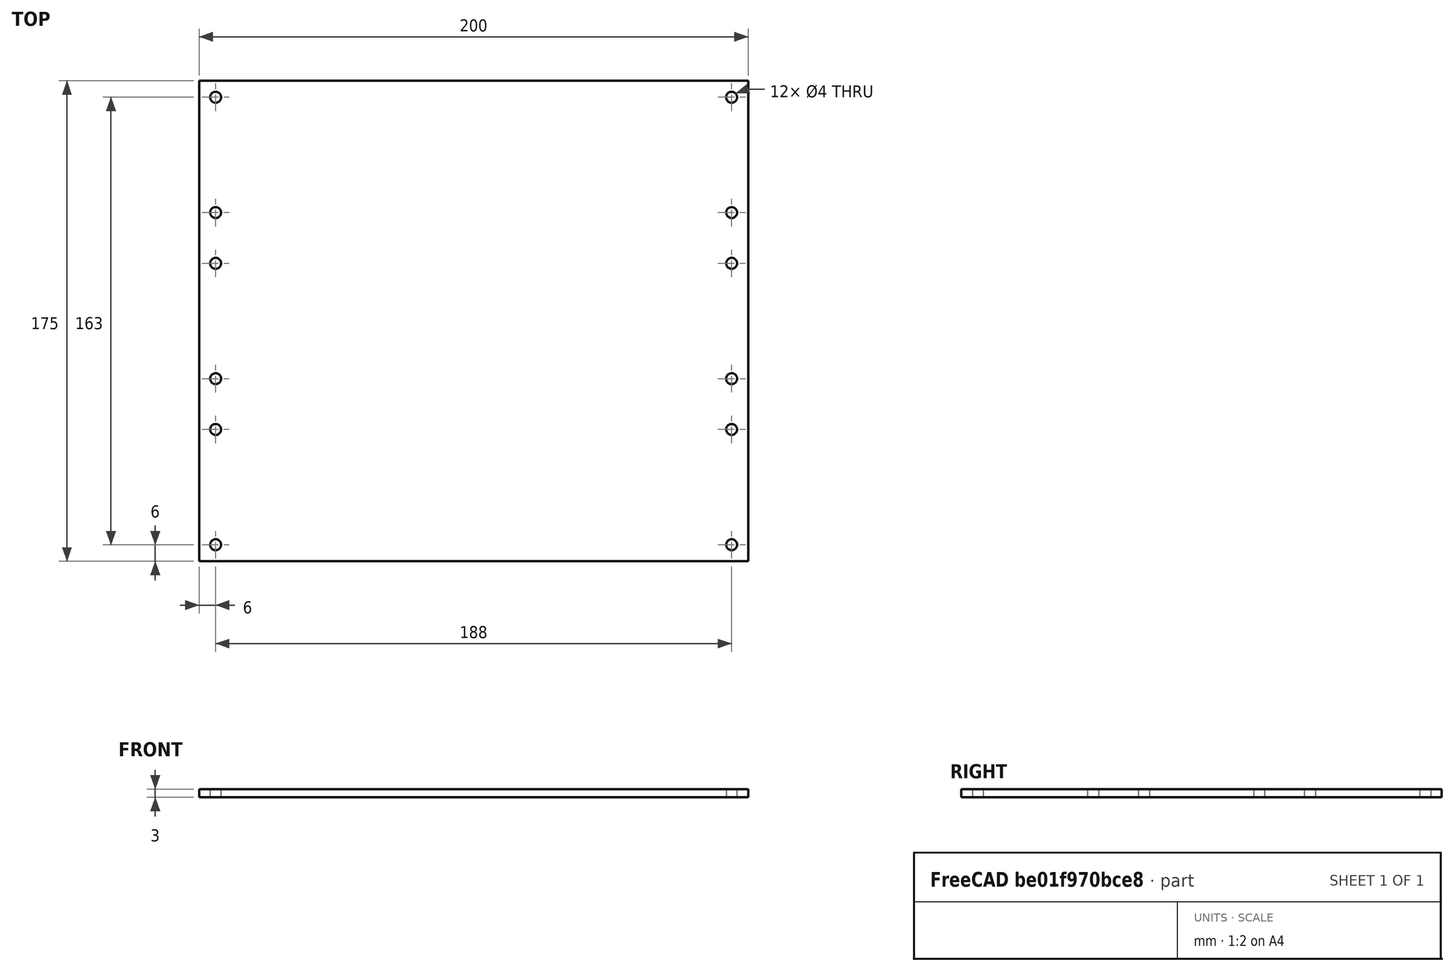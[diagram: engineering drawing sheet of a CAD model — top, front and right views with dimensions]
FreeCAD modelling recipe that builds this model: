
FCSTD DOCUMENT  (FreeCAD 1.1R38728 (Git))
Label: AuxPower1U Aluminium Plate
License: All rights reserved
LicenseURL: https://en.wikipedia.org/wiki/All_rights_reserved
objects: Sketcher::SketchObject×1, PartDesign::Pad×1, PartDesign::Body×1
note: 6 computed .brp shape members not serialized (recipe doc carries the construction recipe); baked Part::Feature solids carry a one-line shape summary decoded from their .brp

FEATURE [Sketcher::SketchObject] Sketch
  ArcFitTolerance = 0
  AttachmentSupport = -> [XY_Plane]
  FullyConstrained = true
  MakeInternals = false
  MapMode = 5
  sketch-geometry (16):
    g0: LineSegment StartX=0 StartY=0 StartZ=0 EndX=200 EndY=0 EndZ=0
    g1: LineSegment StartX=200 StartY=0 StartZ=0 EndX=200 EndY=175 EndZ=0
    g2: LineSegment StartX=200 StartY=175 StartZ=0 EndX=0 EndY=175 EndZ=0
    g3: LineSegment StartX=0 StartY=175 StartZ=0 EndX=0 EndY=0 EndZ=0
    g4: Circle CenterX=6 CenterY=48 CenterZ=0 NormalX=0 NormalY=0 NormalZ=1 AngleXU=0 Radius=2
    g5: Circle CenterX=6 CenterY=6 CenterZ=0 NormalX=0 NormalY=0 NormalZ=1 AngleXU=0 Radius=2
    g6: Circle CenterX=194 CenterY=48 CenterZ=0 NormalX=0 NormalY=0 NormalZ=1 AngleXU=0 Radius=2
    g7: Circle CenterX=194 CenterY=6 CenterZ=0 NormalX=0 NormalY=0 NormalZ=1 AngleXU=0 Radius=2
    g8: Circle CenterX=6 CenterY=169 CenterZ=0 NormalX=0 NormalY=0 NormalZ=1 AngleXU=0 Radius=2
    g9: Circle CenterX=6 CenterY=127 CenterZ=0 NormalX=0 NormalY=0 NormalZ=1 AngleXU=0 Radius=2
    g10: Circle CenterX=6 CenterY=108.5 CenterZ=0 NormalX=0 NormalY=0 NormalZ=1 AngleXU=0 Radius=2
    g11: Circle CenterX=6 CenterY=66.5 CenterZ=0 NormalX=0 NormalY=0 NormalZ=1 AngleXU=0 Radius=2
    g12: Circle CenterX=194 CenterY=108.5 CenterZ=0 NormalX=0 NormalY=0 NormalZ=1 AngleXU=0 Radius=2
    g13: Circle CenterX=194 CenterY=66.5 CenterZ=0 NormalX=0 NormalY=0 NormalZ=1 AngleXU=0 Radius=2
    g14: Circle CenterX=194 CenterY=169 CenterZ=0 NormalX=0 NormalY=0 NormalZ=1 AngleXU=0 Radius=2
    g15: Circle CenterX=194 CenterY=127 CenterZ=0 NormalX=0 NormalY=0 NormalZ=1 AngleXU=0 Radius=2
  constraints (47):
    c: Coincident(g0,g1)
    c: Coincident(g1,g2)
    c: Coincident(g2,g3)
    c: Coincident(g3,g0)
    c: Horizontal(g0)
    c: Horizontal(g2)
    c: Vertical(g1)
    c: Vertical(g3)
    c: Coincident(g0,g-1)
    c: DistanceX(g2,g2) = 200  'Width'
    c: DistanceY(g3,g3) = 175  'Height'
    c: DistanceY(g5,g4) = 42
    c: DistanceX(g5,g4) = 0
    c: DistanceY(g7,g6) = 42
    c: DistanceX(g7,g6) = 0
    c: DistanceY(g5,g7) = 0
    c: DistanceX(g5,g7) = 188
    c: DistanceX(g0,g5) = 6
    c: DistanceY(g0,g5) = 6
    c: DistanceY(g9,g8) = 42
    c: DistanceY(g11,g10) = 42
    c: DistanceY(g13,g12) = 42
    c: Vertical(g13,g12)
    c: Vertical(g10,g11)
    c: Vertical(g9,g8)
    c: Vertical(g14,g15)
    c: DistanceY(g15,g14) = 42
    c: DistanceX(g9,g15) = 188
    c: DistanceX(g11,g13) = 188
    c: Vertical(g6,g13)
    c: Vertical(g12,g15)
    c: DistanceY(g0,g8) = 169
    c: Horizontal(g9,g15)
    c: Horizontal(g13,g11)
    c: DistanceY(g0,g11) = 66.5
    c: Equal(g5,g4)
    c: Equal(g5,g6)
    c: Equal(g5,g7)
    c: Equal(g5,g10)
    c: Equal(g5,g8)
    c: Equal(g5,g9)
    c: Equal(g5,g11)
    c: Equal(g5,g13)
    c: Equal(g5,g14)
    c: Equal(g5,g15)
    c: Equal(g5,g12)
    c: Diameter(g5) = 4
FEATURE [PartDesign::Pad] Pad
  Direction = (0,0,1)
  Length = 3
  Length2 = 10
  Profile = -> Sketch
  ReferenceAxis = -> Sketch [N_Axis]
  Refine = true
  Suppressed = false
  Type = 0
FEATURE [PartDesign::Body] Body
  AllowCompound = false
  Group = -> [Sketch,Pad]
  Origin = -> Origin
  Tip = -> Pad
